# Revit family: QF_Summit_ACFF436L_General_Purpose_Healthcare_Freezer
name_source: partatom
category: Specialty Equipment
units: mm (PartAtom-declared; Revit-internal decimal feet)

## family parameters
Always vertical = Yes
Cut with Voids When Loaded = No
Part Type = Normal
Room Calculation Point = No
Round Connector Dimension = Use Diameter
Shared = No
Work Plane-Based = No

## types (1)
- QF_Summit_ACFF436L_General_Purpose_Healthcare_Freezer
    Apparent Power = 518 VA
    Conn Conduit = Yes
    Cycle = 60 Hz
    Default Elevation = 0"
    Depth = 29 3/4"
    Description = General Purpose Healthcare Freezer
    Elec Conn Connection Height = 0"
    Elec Conn RI Height = 0"
    FL Amps = 5 A
    Foodservice Equipment Identifier = Yes
    Height = 81 1/2"
    Identify Quantity as Lot = Yes
    Length = 54 1/4"
    Manufacturer = Summit
    Max Overcurrent Protection = 0 A
    Min Ckt Ampacity = 0 A
    Model = ACFF436L
    Number of Poles = 1
    Phase = 1
    Volts = 115 V
    Watts = 518 W
    Weight in Pounds = 428

## geometry (parser evidence)
native form markers: Sweep x5
no freeform markers — native parametric forms only
